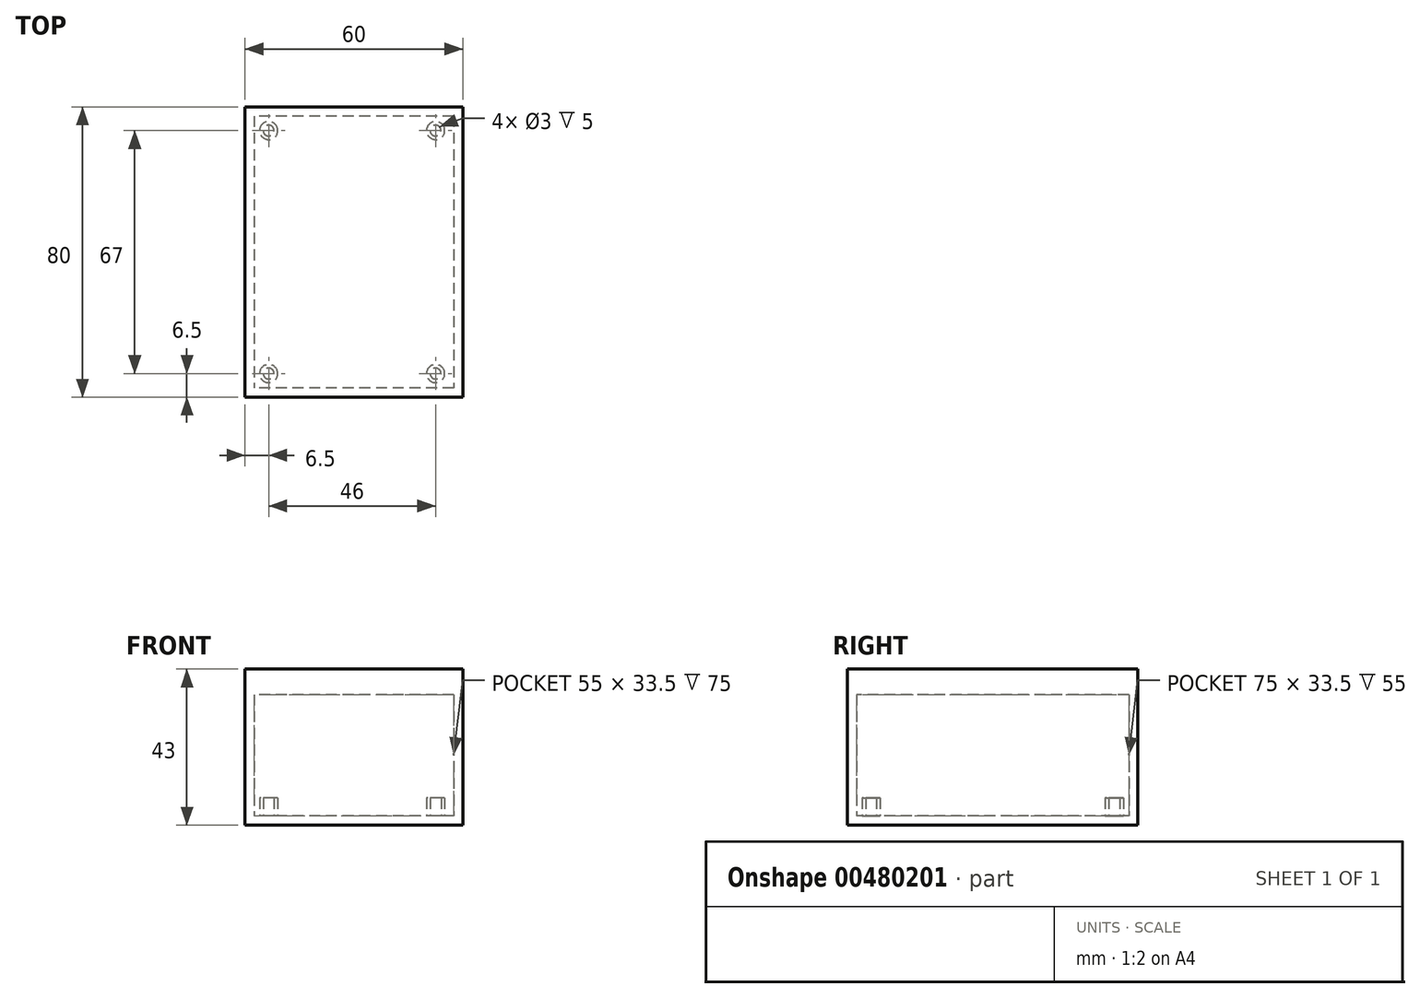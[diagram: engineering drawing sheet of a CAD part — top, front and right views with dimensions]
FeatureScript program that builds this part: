
annotation { "Feature Type Name" : "Feature", "Feature Type Description" : "" }
export const myFeature = defineFeature(function(context is Context, id is Id, definition is map)
    precondition{}
    {
        {
            var Q0;
            Q0=qCreatedBy(makeId("Top.planeOp"),FACE);
            var sketch = newSketch(context, id + "F0", { "sketchPlane" : qUnion([Q0])});
            skLineSegment(sketch, "E0.bottom", {"start": v(30, 40) * mm, "end": v(-30, 40) * mm});
            skLineSegment(sketch, "E0.top", {"start": v(30, -40) * mm, "end": v(-30, -40) * mm});
            skLineSegment(sketch, "E0.left", {"start": v(30, 40) * mm, "end": v(30, -40) * mm});
            skLineSegment(sketch, "E0.right", {"start": v(-30, 40) * mm, "end": v(-30, -40) * mm});
            skPoint(sketch, "E0.middle", {"position": v(0, 0) * mm});
            skSolve(sketch);
        }
        {
            var Q0;
            Q0 = qSketchRegion(id + "F0", true);
            extrude(context, id + "F1", {"entities" : qUnion([Q0]), "depth" : 40 * mm});
        }
        {
            var Q0;
            Q0=makeQuery(id+"F1.opExtrude","CAP_FACE",FACE,{"disambiguationData":[OSD([sQuery(id+"F0.wireOp",EDGE,"E0.bottom"),sQuery(id+"F0.wireOp",EDGE,"E0.top"),sQuery(id+"F0.wireOp",EDGE,"E0.left"),sQuery(id+"F0.wireOp",EDGE,"E0.right")])],"isStart":false});
            shell(context, id + "F2", {"entities" : qUnion([Q0]), "thickness" : 2.5 * mm});
        }
        {
            var Q0;
            Q0=makeQuery(id+"F1.opExtrude","CAP_FACE",FACE,{"disambiguationData":[OSD([sQuery(id+"F0.wireOp",EDGE,"E0.bottom"),sQuery(id+"F0.wireOp",EDGE,"E0.top"),sQuery(id+"F0.wireOp",EDGE,"E0.left"),sQuery(id+"F0.wireOp",EDGE,"E0.right")])],"isStart":false});
            var sketch = newSketch(context, id + "F3", { "sketchPlane" : qUnion([Q0])});
            skLineSegment(sketch, "E1.bottom", {"start": v(-30, -40) * mm, "end": v(30, -40) * mm});
            skLineSegment(sketch, "E1.top", {"start": v(-30, 40) * mm, "end": v(30, 40) * mm});
            skLineSegment(sketch, "E1.left", {"start": v(-30, -40) * mm, "end": v(-30, 40) * mm});
            skLineSegment(sketch, "E1.right", {"start": v(30, -40) * mm, "end": v(30, 40) * mm});
            skLineSegment(sketch, "E2.bottom", {"start": v(-27.5, -37.5) * mm, "end": v(27.5, -37.5) * mm});
            skLineSegment(sketch, "E2.top", {"start": v(-27.5, 37.5) * mm, "end": v(27.5, 37.5) * mm});
            skLineSegment(sketch, "E2.left", {"start": v(-27.5, -37.5) * mm, "end": v(-27.5, 37.5) * mm});
            skLineSegment(sketch, "E2.right", {"start": v(27.5, -37.5) * mm, "end": v(27.5, 37.5) * mm});
            skSolve(sketch);
        }
        {
            var Q0;
            Q0=makeQuery(id+"F3.imprint","IMPRINT",FACE,{"disambiguationData":[TD([[makeQuery(id+"F3.imprint","IMPRINT",EDGE,{"derivedFrom":sQuery(id+"F3.wireOp",EDGE,"E1.bottom")}),-1.0]])]});
            var Q1;
            Q1=makeQuery(id+"F3.imprint","IMPRINT",FACE,{"disambiguationData":[TD([[makeQuery(id+"F3.imprint","IMPRINT",EDGE,{"derivedFrom":sQuery(id+"F3.wireOp",EDGE,"E2.bottom")}),-1.0]])]});
            extrude(context, id + "F4", {"entities" : qUnion([Q0, Q1]), "depth" : 3 * mm});
        }
        {
            var Q0;
            Q0=makeQuery(id+"F3.imprint","IMPRINT",FACE,{"disambiguationData":[TD([[makeQuery(id+"F3.imprint","IMPRINT",EDGE,{"derivedFrom":sQuery(id+"F3.wireOp",EDGE,"E2.bottom")}),-1.0]])]});
            extrude(context, id + "F5", {"entities" : qUnion([Q0]), "operationType" : NewBodyOperationType.ADD, "oppositeDirection" : true, "depth" : 4 * mm});
        }
        {
            var Q0;
            Q0=makeQuery(id+"F2.opShell","OFFSET_FACE",FACE,{"disambiguationData":[OSD([sQuery(id+"F0.wireOp",EDGE,"E0.bottom"),sQuery(id+"F0.wireOp",EDGE,"E0.top"),sQuery(id+"F0.wireOp",EDGE,"E0.left"),sQuery(id+"F0.wireOp",EDGE,"E0.right")])]});
            var sketch = newSketch(context, id + "F6", { "sketchPlane" : qUnion([Q0])});
            skCircle(sketch, "E3", {"center": v(22.5, -33.5) * mm, "radius": 1.5 * mm});
            skCircle(sketch, "E4", {"center": v(22.5, 33.5) * mm, "radius": 1.5 * mm});
            skCircle(sketch, "E5", {"center": v(-23.5, 33.5) * mm, "radius": 1.5 * mm});
            skCircle(sketch, "E6", {"center": v(-23.5, -33.5) * mm, "radius": 1.5 * mm});
            skCircle(sketch, "E7", {"center": v(22.5, 33.5) * mm, "radius": 2.5 * mm});
            skCircle(sketch, "E8", {"center": v(22.5, -33.5) * mm, "radius": 2.5 * mm});
            skCircle(sketch, "E9", {"center": v(-23.5, -33.5) * mm, "radius": 2.5 * mm});
            skCircle(sketch, "E10", {"center": v(-23.5, 33.5) * mm, "radius": 2.5 * mm});
            skSolve(sketch);
        }
        {
            var Q0;
            Q0 = qSketchRegion(id + "F6", true);
            extrude(context, id + "F7", {"entities" : qUnion([Q0]), "operationType" : NewBodyOperationType.ADD, "depth" : 5 * mm});
        }
    });
